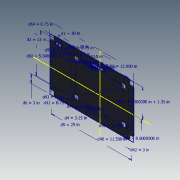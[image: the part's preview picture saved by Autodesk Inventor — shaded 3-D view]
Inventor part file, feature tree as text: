
AUTODESK INVENTOR PART (.ipt)
format: ipt  version: 2020.3 (Build 243373000, 373)  size: 295,424 bytes
history: native  units: in
note: dims shown in document units (in); Inventor stores cm internally (conversion verified against a paired STEP export)
features: hole x6, extrude x3, fillet x3, sketch x2, pattern_linear x1
ambient origin geometry x8: Origin, YZ Plane, XZ Plane, XY Plane, X Axis, Y Axis, Z Axis, Center Point
bodies: Solid1 (feature_tree)
feature tree (15):
  extrude  "Extrusion1"  Depth=30.0in
  hole  "Hole1"  [1 undecoded]
  hole  "Hole2"  [1 undecoded]
  extrude  "Extrusion2"  Depth=1.0in
  fillet  "Fillet1"  Radius=0.25in
  hole  "Hole3"  [1 undecoded]
  hole  "Hole4"  [1 undecoded]
  pattern_linear  "Rectangular Pattern1"  Spacing1=0.25in  [1 undecoded]
  extrude  "Extrusion3"  Depth=17.0in
  fillet  "Fillet2"  Radius=12.0in
  fillet  "Fillet3"  Radius=1.6in
  hole  "Hole5"  [1 undecoded]
  hole  "Hole6"  [1 undecoded]
  sketch  "Sketch2"  dims[d1=30.0in d2=20.5in]
  sketch  "Sketch4"  dims[d3=13.0in d4=3.25in d5=29.0in d6=3.0in d8=0.25in d9=0.0in d10=0.375in d11=0.5in d12=0.375in d13=0.25in d14=0.5635in d15=1.0in d16=0.8108in d17=0.45in d18=0.5in d19=0.375in d20=0.25in d21=0.5635in d22=1.0in d23=0.8108in d24=1.4in d25=0.25in d26=0.0in d27=0.25in d28=17.0in d29=12.0in d30=1.5in d31=0.5in d32=0.375in d33=0.25in d34=0.5635in d35=1.0in d36=0.8108in d37=1.6in d38=12.0in d39=10.25in d40=11.5in d41=0.75in d42=3.0in d43=3.0in d44=12.0in d46=12.0in d47=2.0in d48=1.25in d49=6.0in d50=0.123in d51=0.75in d52=0.375in d53=0.25in d54=0.5635in d55=1.0in d56=0.8108in d57=1.5748in d59=2.0in d60=5.6in d61=8.6in d62=1.4in d63=1.6in d64=0.75in d65=1.4in d66=2.0in d67=1.0in d68=15.0in d69=2.0in d70=0.0in d71=0.0in d72=0.125in d73=0.125in d74=3.0in d75=3.0in d76=3.0in d77=3.0in d78=0.123in d79=0.75in d80=0.375in d81=0.25in d82=0.5635in d83=1.0in d84=0.8108in d85=3.0in d86=3.0in d87=4.0in d88=3.0in d89=1.5in d90=1.5in d91=1.5in d92=1.5in d95=0.5in d96=1.5in d97=1.5in d98=1.0in d99=2.0in d100=0.75in d101=1.5748in d103=0.5in d104=0.3937in d106=1.0in d108=0.3125in d109=0.75in d110=0.375in d111=0.25in d112=0.5635in d113=1.0in d114=0.8108in]
note: 7 required parameter values undecoded (feature->parameter linkage not recoverable at this tier; creation-order binding heuristic only, values carry confidence <= 0.55)
